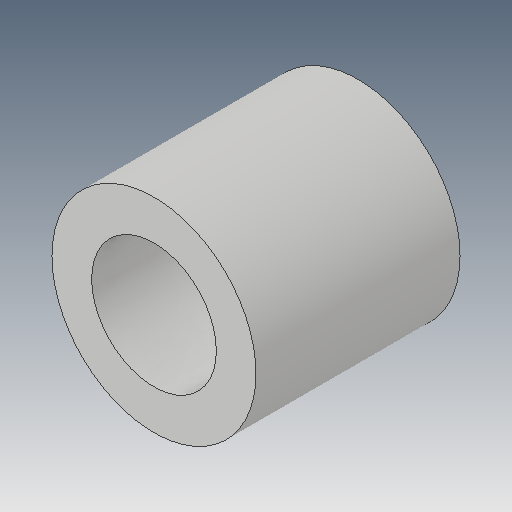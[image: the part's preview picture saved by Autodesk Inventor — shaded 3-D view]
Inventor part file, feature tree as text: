
AUTODESK INVENTOR PART (.ipt)
format: ipt  version: 2017 (Build 210142000, 142)  size: 102,400 bytes
history: native  units: mm
features: extrude x1, sketch x1
ambient origin geometry x8: Origin, YZ Plane, XZ Plane, XY Plane, X Axis, Y Axis, Z Axis, Center Point
bodies: Solid1 (feature_tree)
feature tree (2):
  extrude  "Extrusion1"  Depth=9.0mm
  sketch  "Sketch1"  dims[d0=5.5mm d1=9.0mm d2=9.0mm d3=0.0mm]
